# Revit family: Lighting-Industrial-GEWISS-ESALITE-HB-HIGHBAYS-LED_6K_EMERGENCY
name_source: partatom
category: Apparecchi per illuminazione
units: mm (PartAtom-declared; Revit-internal decimal feet)

## family parameters
Condiviso = No
Host = Superficie
Punto di calcolo locali = Sì
Quota connettore circolare = Usa diametro
Sorgente d'illuminazione = No
Taglio con vuoti quando caricato = No
Tipo di parte = Normale

## types (1)
- Lighting-Industrial-GEWISS-ESALITE-HB-HIGHBAYS-LED_6K_EMERGENCY
    Application = Internal
    Autonomy = 3H
    Catalogue = LIGHTING
    Catalogue Range = ESALITE HB - 6K
    Colour = Grey RAL 9006 + 7035
    Colour temperature: = 4000 K (CRI>80)
    DIN 18032-3 certification = No
    Description: = Esalite HB 6k with lens and Emergency 3h – 4000K (CRI80)
    Descrizione = KIT EMERGENZA 3H ESALITE 12-16-20K
    Device with reduced surface temperature = Complying
    Driver type = Driver Dali
    Efficiency class of integrated LEDs = A ÷ A++
    Electrocod = 2444
    Glow Wire Test = 650°C
    IDF = 22ae4d23-6439-4741-b737-d04c9a983d65
    IDT = e1623446787a4785a8c69eeae9ffe9d2
    IP degree = IP55
    Immagine tipo = ESALITE_HB.jpg
    Insulation class = I
    LED current = 0,6A
    LED current. = 0,599999999999999A
    Lamp- = LED - Not replaceable
    Life time L90B10 (Tq 25°C) = 100000H
    Life time L90B10 (Tq 50°C) = 55000H
    Lumen output (lm) = 6700
    Lumen output (lm): = 6700
    Luminous flux in emerg. (lm) = 650
    Modello = GWS6911
    Nominal flux (lm) = 7200
    Numero poli = 1
    Operating temperature: = 0 ÷ +40 °C
    Optic = 90°
    Potenza di sitema = Wxxx
    Produttore = GEWISS S.p.A.
    Prospetto di default = 1219 mm
    SEO = High bay
    Shield type = Plastic
    Shock resistance = IK06
    System power = 60W
    Technical sheet = https://www.gewiss.com
    Type of light source = LED - Not replaceable
    Typology = Emergency
    URL = https://www.gewiss.com
    V = 0 V
    Version file RFA = 20.11
    Version type = Emergency
    Versions = 4000K natural light
    Voltage- = 220/240 V - 50/60 Hz
    Warranty = 5 years
    Weight (kg): = 4,5
